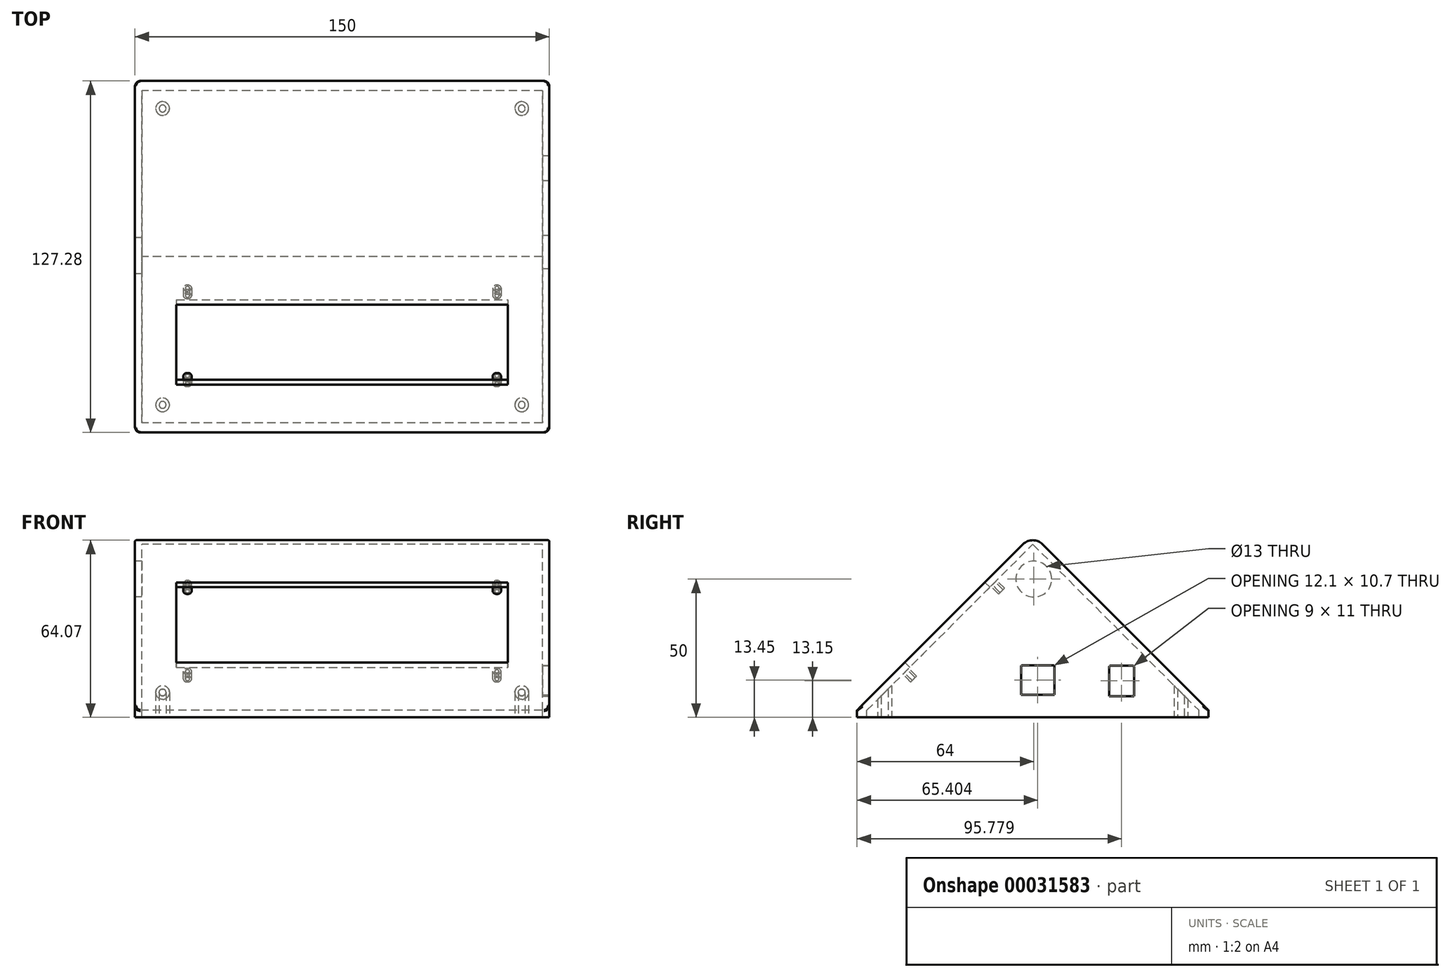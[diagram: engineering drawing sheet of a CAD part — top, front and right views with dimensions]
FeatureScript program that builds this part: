
annotation { "Feature Type Name" : "Feature", "Feature Type Description" : "" }
export const myFeature = defineFeature(function(context is Context, id is Id, definition is map)
    precondition{}
    {
        {
            var Q0;
            Q0=qCreatedBy(makeId("Right.planeOp"),FACE);
            var sketch = newSketch(context, id + "F0", { "sketchPlane" : qUnion([Q0])});
            skLineSegment(sketch, "E0", {"start": v(0, 0) * mm, "end": v(63.64, 63.64) * mm});
            skLineSegment(sketch, "E1", {"start": v(63.64, 63.64) * mm, "end": v(127.28, 0) * mm});
            skLineSegment(sketch, "E2", {"start": v(127.28, 0) * mm, "end": v(0, 0) * mm});
            skSolve(sketch);
        }
        {
            var Q0;
            Q0=qSketchRegion(id+"F0",true);
            extrude(context, id + "F1", {"entities" : qUnion([Q0]), "depth" : 150 * mm});
        }
        {
            var Q0;
            Q0=makeQuery(id+"F1.opExtrude","SWEPT_FACE",FACE,{"disambiguationData":[OSD([sQuery(id+"F0.wireOp",EDGE,"E2")])]});
            shell(context, id + "F2", {"entities" : qUnion([Q0]), "thickness" : 2.5 * mm});
        }
        {
            var Q0;
            Q0=makeQuery(id+"F1.opExtrude","SWEPT_FACE",FACE,{"disambiguationData":[OSD([sQuery(id+"F0.wireOp",EDGE,"E0")])]});
            cPlane(context, id + "F3", {"entities" : qUnion([Q0]), "cplaneType" : CPlaneType.OFFSET, "offset" : 0 * mm, "width" : 150 * mm, "height" : 150 * mm});
        }
        {
            var Q0;
            Q0=qCreatedBy(id+"F3.planeOp",FACE);
            var sketch = newSketch(context, id + "F4", { "sketchPlane" : qUnion([Q0])});
            skLineSegment(sketch, "E3.bottom", {"start": v(15, 65.5) * mm, "end": v(135, 65.5) * mm});
            skLineSegment(sketch, "E3.top", {"start": v(15, 24.5) * mm, "end": v(135, 24.5) * mm});
            skLineSegment(sketch, "E3.left", {"start": v(15, 65.5) * mm, "end": v(15, 24.5) * mm});
            skLineSegment(sketch, "E3.right", {"start": v(135, 65.5) * mm, "end": v(135, 24.5) * mm});
            skLineSegment(sketch, "E4", {"start": v(15, 45) * mm, "end": v(91.25, 45) * mm, "construction": true});
            skSolve(sketch);
        }
        {
            var Q0;
            Q0=qSketchRegion(id+"F4",true);
            extrude(context, id + "F5", {"entities" : qUnion([Q0]), "operationType" : NewBodyOperationType.REMOVE, "oppositeDirection" : true, "depth" : 3 * mm});
        }
        {
            var Q0;
            Q0=makeQuery(id+"F1.opExtrude","SWEPT_EDGE",EDGE,{"disambiguationData":[OSD([sQuery(id+"F0.wireOp",EDGE,"E0"),sQuery(id+"F0.wireOp",EDGE,"E1")])]});
            fillet(context, id + "F6", {"entities" : qUnion([Q0]), "radius" : 5 * mm, "tangentPropagation" : true, "allowEdgeOverflow" : false});
        }
        {
            var Q0;
            Q0=makeQuery(id+"F1.opExtrude","CAP_FACE",FACE,{"disambiguationData":[OSD([sQuery(id+"F0.wireOp",EDGE,"E0"),sQuery(id+"F0.wireOp",EDGE,"E1"),sQuery(id+"F0.wireOp",EDGE,"E2")])],"isStart":false});
            var sketch = newSketch(context, id + "F7", { "sketchPlane" : qUnion([Q0])});
            skCircle(sketch, "E5", {"center": v(70, 8) * mm, "radius": 6 * mm, "construction": true});
            skLineSegment(sketch, "E6.bottom", {"start": v(91.28, 5.15) * mm, "end": v(100.28, 5.15) * mm});
            skLineSegment(sketch, "E6.top", {"start": v(91.28, 16.15) * mm, "end": v(100.28, 16.15) * mm});
            skLineSegment(sketch, "E6.left", {"start": v(91.28, 5.15) * mm, "end": v(91.28, 16.15) * mm});
            skLineSegment(sketch, "E6.right", {"start": v(100.28, 5.15) * mm, "end": v(100.28, 16.15) * mm});
            skLineSegment(sketch, "E7.bottom", {"start": v(59.35, 16.3) * mm, "end": v(71.45, 16.3) * mm});
            skLineSegment(sketch, "E7.top", {"start": v(59.35, 5.6) * mm, "end": v(71.45, 5.6) * mm});
            skLineSegment(sketch, "E7.left", {"start": v(59.35, 16.3) * mm, "end": v(59.35, 5.6) * mm});
            skLineSegment(sketch, "E7.right", {"start": v(71.45, 16.3) * mm, "end": v(71.45, 5.6) * mm});
            skSolve(sketch);
        }
        {
            var Q0;
            Q0=makeQuery(id+"F1.opExtrude","SWEPT_FACE",FACE,{"disambiguationData":[OSD([sQuery(id+"F0.wireOp",EDGE,"E0")])]});
            var sketch = newSketch(context, id + "F8", { "sketchPlane" : qUnion([Q0])});
            skCircle(sketch, "E8", {"center": v(131, 22.5) * mm, "radius": 0.75 * mm});
            skCircle(sketch, "E9", {"center": v(131, 67.5) * mm, "radius": 0.75 * mm});
            skPoint(sketch, "E10.endSnap0", {"position": v(75, 65.5) * mm});
            skCircle(sketch, "E11", {"center": v(131, 67.5) * mm, "radius": 1.5 * mm});
            skCircle(sketch, "E12", {"center": v(131, 22.5) * mm, "radius": 1.5 * mm});
            skCircle(sketch, "E13", {"center": v(19, 67.5) * mm, "radius": 0.75 * mm});
            skCircle(sketch, "E14", {"center": v(19, 67.5) * mm, "radius": 1.5 * mm});
            skCircle(sketch, "E15", {"center": v(19, 22.5) * mm, "radius": 0.75 * mm});
            skCircle(sketch, "E16", {"center": v(19, 22.5) * mm, "radius": 1.5 * mm});
            skSolve(sketch);
        }
        {
            var Q0;
            Q0=qSketchRegion(id+"F8",true);
            extrude(context, id + "F9", {"entities" : qUnion([Q0]), "operationType" : NewBodyOperationType.ADD, "oppositeDirection" : true, "depth" : 6.5 * mm});
        }
        {
            var Q0;
            Q0=makeQuery(id+"F1.opExtrude","SWEPT_FACE",FACE,{"disambiguationData":[OSD([sQuery(id+"F0.wireOp",EDGE,"E2")])]});
            var sketch = newSketch(context, id + "F10", { "sketchPlane" : qUnion([Q0])});
            skCircle(sketch, "E17", {"center": v(10, -10) * mm, "radius": 1.5 * mm});
            skCircle(sketch, "E18", {"center": v(10, -10) * mm, "radius": 2.5 * mm});
            skSolve(sketch);
        }
        {
            var Q0;
            Q0=qSketchRegion(id+"F10",true);
            var Q1;
            Q1=makeQuery(id+"F1.opExtrude","SWEPT_FACE",FACE,{"disambiguationData":[OSD([sQuery(id+"F0.wireOp",EDGE,"E0")])]});
            extrude(context, id + "F11", {"entities" : qUnion([Q0]), "operationType" : NewBodyOperationType.ADD, "endBound" : BoundingType.UP_TO_SURFACE, "oppositeDirection" : true, "endBoundEntityFace" : qUnion([Q1]), "depth" : 25 * mm});
        }
        {
            var Q0;
            Q0=makeQuery(id+"F1.opExtrude","SWEPT_FACE",FACE,{"disambiguationData":[OSD([sQuery(id+"F0.wireOp",EDGE,"E2")])]});
            var sketch = newSketch(context, id + "F12", { "sketchPlane" : qUnion([Q0])});
            skCircle(sketch, "E19", {"center": v(10, -117.28) * mm, "radius": 2.5 * mm, "construction": true});
            skCircle(sketch, "E20", {"center": v(10, -117.28) * mm, "radius": 1.5 * mm, "construction": true});
            skCircle(sketch, "E21", {"center": v(140, -117.28) * mm, "radius": 1.5 * mm, "construction": true});
            skCircle(sketch, "E22", {"center": v(140, -117.28) * mm, "radius": 2.5 * mm, "construction": true});
            skCircle(sketch, "E23", {"center": v(10, -10) * mm, "radius": 1.25 * mm});
            skCircle(sketch, "E24", {"center": v(10, -10) * mm, "radius": 2.5 * mm});
            skCircle(sketch, "E25", {"center": v(140, -10) * mm, "radius": 1.25 * mm});
            skCircle(sketch, "E26", {"center": v(140, -10) * mm, "radius": 2.5 * mm});
            skSolve(sketch);
        }
        {
            var Q0;
            Q0=qSketchRegion(id+"F12",true);
            var Q1;
            {var subQ1=sQuery(id+"F0.wireOp",EDGE,"E2");var subQ3=sQuery(id+"F0.wireOp",EDGE,"E0");var subQ13=makeQuery(id+"F1.opExtrude","SWEPT_FACE",FACE,{"disambiguationData":[OSD([subQ1])]});Q1=makeQuery(id+"F11.boolean.opBoolean","SPLIT",FACE,{"disambiguationData":[TD([subQ13])],"derivedFrom":makeQuery(id+"F9.boolean.opBoolean","SPLIT",FACE,{"disambiguationData":[TD([subQ13])],"derivedFrom":makeQuery(id+"F2.opShell","OFFSET_FACE",FACE,{"disambiguationData":[OSD([subQ3])]})})});}
            extrude(context, id + "F13", {"entities" : qUnion([Q0]), "operationType" : NewBodyOperationType.ADD, "endBound" : BoundingType.UP_TO_SURFACE, "oppositeDirection" : true, "endBoundEntityFace" : qUnion([Q1]), "depth" : 25 * mm});
        }
        {
            var Q0;
            Q0=makeQuery(id+"F1.opExtrude","SWEPT_FACE",FACE,{"disambiguationData":[OSD([sQuery(id+"F0.wireOp",EDGE,"E2")])]});
            var sketch = newSketch(context, id + "F14", { "sketchPlane" : qUnion([Q0])});
            skLineSegment(sketch, "E27.bottom", {"start": v(0, 0) * mm, "end": v(150, 0) * mm});
            skLineSegment(sketch, "E27.top", {"start": v(0, -127.28) * mm, "end": v(150, -127.28) * mm});
            skLineSegment(sketch, "E27.left", {"start": v(0, 0) * mm, "end": v(0, -127.28) * mm});
            skLineSegment(sketch, "E27.right", {"start": v(150, 0) * mm, "end": v(150, -127.28) * mm});
            skLineSegment(sketch, "E28.bottom", {"start": v(147.5, -123.74) * mm, "end": v(2.5, -123.74) * mm});
            skLineSegment(sketch, "E28.top", {"start": v(147.5, -3.54) * mm, "end": v(2.5, -3.54) * mm});
            skLineSegment(sketch, "E28.left", {"start": v(147.5, -123.74) * mm, "end": v(147.5, -3.54) * mm});
            skLineSegment(sketch, "E28.right", {"start": v(2.5, -123.74) * mm, "end": v(2.5, -3.54) * mm});
            skSolve(sketch);
        }
        {
            var Q0;
            Q0=qSketchRegion(id+"F14",true);
            extrude(context, id + "F15", {"entities" : qUnion([Q0]), "operationType" : NewBodyOperationType.ADD, "depth" : 2.5 * mm});
        }
        {
            var Q0;
            Q0=qCreatedBy(makeId("Top.planeOp"),FACE);
            var sketch = newSketch(context, id + "F16", { "sketchPlane" : qUnion([Q0])});
            skCircle(sketch, "E29", {"center": v(10, 117.28) * mm, "radius": 1.25 * mm});
            skCircle(sketch, "E30.0", {"center": v(10, 10) * mm, "radius": 2.5 * mm, "construction": true});
            skCircle(sketch, "E31", {"center": v(10, 117.28) * mm, "radius": 2.5 * mm});
            skCircle(sketch, "E32", {"center": v(140, 117.28) * mm, "radius": 1.25 * mm});
            skCircle(sketch, "E33", {"center": v(140, 117.28) * mm, "radius": 2.5 * mm});
            skCircle(sketch, "E34.0", {"center": v(140, 10) * mm, "radius": 1.25 * mm});
            skSolve(sketch);
        }
        {
            var Q0;
            Q0=makeQuery(id+"F16.imprint","IMPRINT",FACE,{"disambiguationData":[TD([[makeQuery(id+"F16.imprint","IMPRINT",EDGE,{"derivedFrom":sQuery(id+"F16.wireOp",EDGE,"E32")}),-1.0]])]});
            var Q1;
            Q1=makeQuery(id+"F16.imprint","IMPRINT",FACE,{"disambiguationData":[TD([[makeQuery(id+"F16.imprint","IMPRINT",EDGE,{"derivedFrom":sQuery(id+"F16.wireOp",EDGE,"E29")}),-1.0]])]});
            var Q2;
            Q2=makeQuery(id+"F2.opShell","OFFSET_FACE",FACE,{"disambiguationData":[OSD([sQuery(id+"F0.wireOp",EDGE,"E1")])]});
            extrude(context, id + "F17", {"entities" : qUnion([Q0, Q1]), "operationType" : NewBodyOperationType.ADD, "endBound" : BoundingType.UP_TO_SURFACE, "endBoundEntityFace" : qUnion([Q2]), "depth" : 25 * mm});
        }
        {
            var Q0;
            Q0=makeQuery(id+"F15.opExtrude","SWEPT_EDGE",EDGE,{"disambiguationData":[OSD([sQuery(id+"F14.wireOp",EDGE,"E27.top"),sQuery(id+"F14.wireOp",EDGE,"E27.right")])]});
            var Q1;
            Q1=makeQuery(id+"F15.opExtrude","SWEPT_EDGE",EDGE,{"disambiguationData":[OSD([sQuery(id+"F14.wireOp",EDGE,"E27.bottom"),sQuery(id+"F14.wireOp",EDGE,"E27.right")])]});
            var Q2;
            Q2=makeQuery(id+"F15.opExtrude","SWEPT_EDGE",EDGE,{"disambiguationData":[OSD([sQuery(id+"F14.wireOp",EDGE,"E27.bottom"),sQuery(id+"F14.wireOp",EDGE,"E27.left")])]});
            var Q3;
            Q3=makeQuery(id+"F15.opExtrude","SWEPT_EDGE",EDGE,{"disambiguationData":[OSD([sQuery(id+"F14.wireOp",EDGE,"E27.top"),sQuery(id+"F14.wireOp",EDGE,"E27.left")])]});
            fillet(context, id + "F18", {"entities" : qUnion([Q0, Q1, Q2, Q3]), "radius" : 2 * mm, "tangentPropagation" : true, "allowEdgeOverflow" : false});
        }
        {
            var Q0;
            Q0=makeQuery(id+"F1.opExtrude","CAP_EDGE",EDGE,{"disambiguationData":[OSD([sQuery(id+"F0.wireOp",EDGE,"E0")])],"isStart":true});
            fillet(context, id + "F19", {"entities" : qUnion([Q0]), "radius" : 0.5 * mm, "tangentPropagation" : true, "allowEdgeOverflow" : false});
        }
        {
            var Q0;
            Q0=qSketchRegion(id+"F7",true);
            extrude(context, id + "F20", {"entities" : qUnion([Q0]), "operationType" : NewBodyOperationType.REMOVE, "oppositeDirection" : true, "depth" : 3 * mm});
        }
        {
            var Q0;
            Q0=makeQuery(id+"F20.boolean.opBoolean","COPY",EDGE,{"derivedFrom":makeQuery(id+"F20.opExtrude","SWEPT_EDGE",EDGE,{"disambiguationData":[OSD([sQuery(id+"F7.wireOp",EDGE,"E6.top"),sQuery(id+"F7.wireOp",EDGE,"E6.left")])]})});
            var Q1;
            Q1=makeQuery(id+"F20.boolean.opBoolean","COPY",EDGE,{"derivedFrom":makeQuery(id+"F20.opExtrude","SWEPT_EDGE",EDGE,{"disambiguationData":[OSD([sQuery(id+"F7.wireOp",EDGE,"E6.top"),sQuery(id+"F7.wireOp",EDGE,"E6.right")])]})});
            fillet(context, id + "F21", {"entities" : qUnion([Q0, Q1]), "radius" : 0.5 * mm, "tangentPropagation" : true, "allowEdgeOverflow" : false});
        }
        {
            var Q0;
            Q0=makeQuery(id+"F20.boolean.opBoolean","COPY",EDGE,{"derivedFrom":makeQuery(id+"F20.opExtrude","SWEPT_EDGE",EDGE,{"disambiguationData":[OSD([sQuery(id+"F7.wireOp",EDGE,"E7.bottom"),sQuery(id+"F7.wireOp",EDGE,"E7.left")])]})});
            var Q1;
            Q1=makeQuery(id+"F20.boolean.opBoolean","COPY",EDGE,{"derivedFrom":makeQuery(id+"F20.opExtrude","SWEPT_EDGE",EDGE,{"disambiguationData":[OSD([sQuery(id+"F7.wireOp",EDGE,"E7.bottom"),sQuery(id+"F7.wireOp",EDGE,"E7.right")])]})});
            fillet(context, id + "F22", {"entities" : qUnion([Q0, Q1]), "radius" : .5 * mm, "tangentPropagation" : true, "allowEdgeOverflow" : false});
        }
        {
            var Q0;
            Q0=makeQuery(id+"F15.boolean.opBoolean","MERGE",FACE,{"derivedFrom":[makeQuery(id+"F1.opExtrude","CAP_FACE",FACE,{"disambiguationData":[OSD([sQuery(id+"F0.wireOp",EDGE,"E0"),sQuery(id+"F0.wireOp",EDGE,"E1"),sQuery(id+"F0.wireOp",EDGE,"E2")])],"isStart":true}),makeQuery(id+"F15.opExtrude","SWEPT_FACE",FACE,{"disambiguationData":[OSD([sQuery(id+"F14.wireOp",EDGE,"E27.left")])]})]});
            var sketch = newSketch(context, id + "F23", { "sketchPlane" : qUnion([Q0])});
            skCircle(sketch, "E35", {"center": v(-64, 47.5) * mm, "radius": 6.5 * mm});
            skSolve(sketch);
        }
        {
            var Q0;
            Q0=makeQuery(id+"F23.imprint","IMPRINT",FACE,{"disambiguationData":[TD([[makeQuery(id+"F23.imprint","IMPRINT",EDGE,{"derivedFrom":sQuery(id+"F23.wireOp",EDGE,"E35")}),1.0]])]});
            var Q1;
            Q1=sQuery(id+"F23.wireOp",EDGE,"E35");
            extrude(context, id + "F24", {"entities" : qUnion([Q0]), "operationType" : NewBodyOperationType.REMOVE, "surfaceEntities" : qUnion([Q1]), "oppositeDirection" : true, "depth" : 2.5 * mm});
        }
        {
            var Q0;
            Q0=makeQuery(id+"F13.opExtrude","CAP_FACE",FACE,{"disambiguationData":[OSD([sQuery(id+"F12.wireOp",EDGE,"E25"),sQuery(id+"F12.wireOp",EDGE,"E26")])],"isStart":true});
            var sketch = newSketch(context, id + "F25", { "sketchPlane" : qUnion([Q0])});
            skCircle(sketch, "E36", {"center": v(140, -10) * mm, "radius": 1.25 * mm});
            skCircle(sketch, "E37.0", {"center": v(10, -10) * mm, "radius": 1.25 * mm});
            skCircle(sketch, "E38.0", {"center": v(10, -10) * mm, "radius": 2.5 * mm});
            skCircle(sketch, "E39.0", {"center": v(140, -10) * mm, "radius": 2.5 * mm});
            skCircle(sketch, "E40.0", {"center": v(10, -117.28) * mm, "radius": 1.25 * mm});
            skCircle(sketch, "E41.0", {"center": v(10, -117.28) * mm, "radius": 2.5 * mm});
            skCircle(sketch, "E42.0", {"center": v(140, -117.28) * mm, "radius": 1.25 * mm});
            skCircle(sketch, "E43.0", {"center": v(140, -117.28) * mm, "radius": 2.5 * mm});
            skSolve(sketch);
        }
        {
            var Q0;
            Q0=qSketchRegion(id+"F25",true);
            extrude(context, id + "F26", {"entities" : qUnion([Q0]), "operationType" : NewBodyOperationType.ADD, "depth" : 2.5 * mm});
        }
    });
